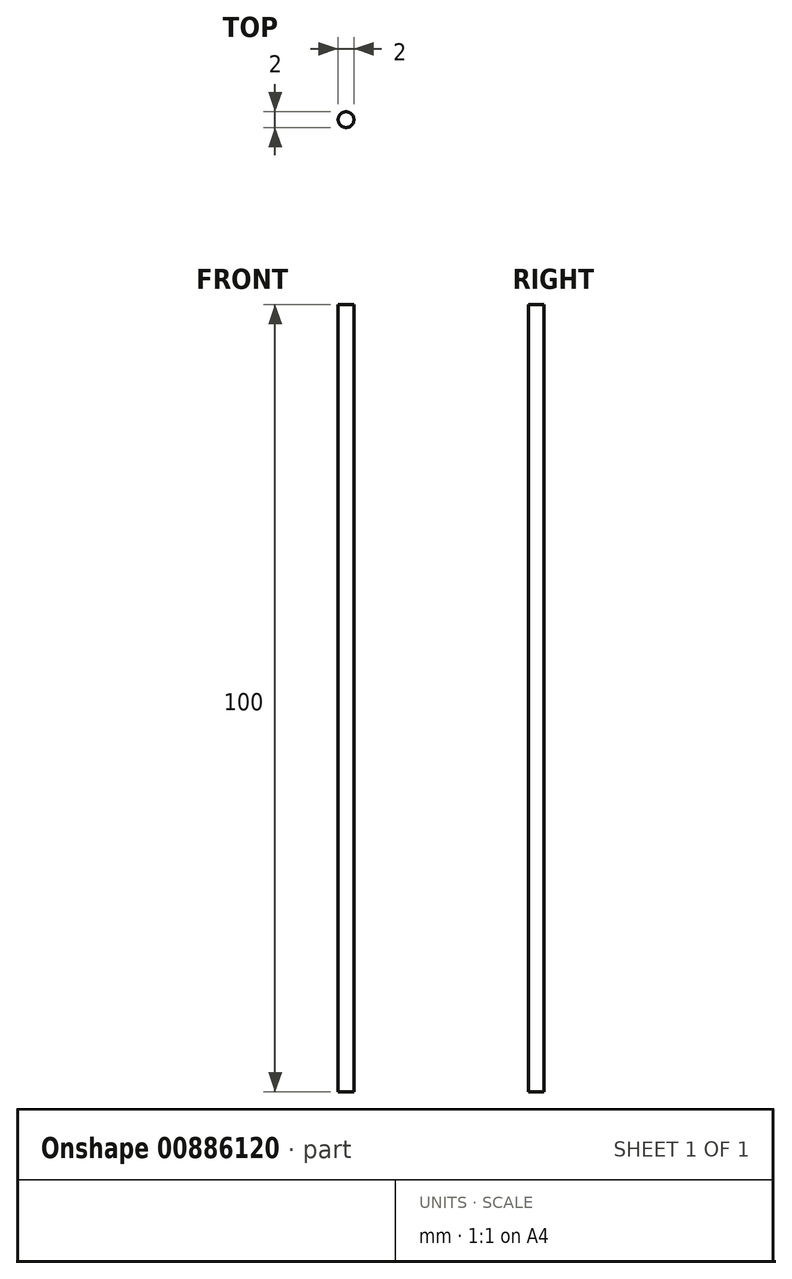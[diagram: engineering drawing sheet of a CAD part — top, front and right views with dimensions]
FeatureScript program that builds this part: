
annotation { "Feature Type Name" : "Feature", "Feature Type Description" : "" }
export const myFeature = defineFeature(function(context is Context, id is Id, definition is map)
    precondition{}
    {
        {
            var Q0;
            Q0=qCreatedBy(makeId("Top.planeOp"),FACE);
            var sketch = newSketch(context, id + "F0", { "sketchPlane" : qUnion([Q0])});
            skCircle(sketch, "E0", {"center": v(-11.7, -14.43) * mm, "radius": 1 * mm});
            skSolve(sketch);
        }
        {
            var Q0;
            Q0 = qSketchRegion(id + "F0", true);
            extrude(context, id + "F1", {"entities" : qUnion([Q0]), "depth" : 100 * mm, "offsetDistance" : 25 * mm});
        }
    });
